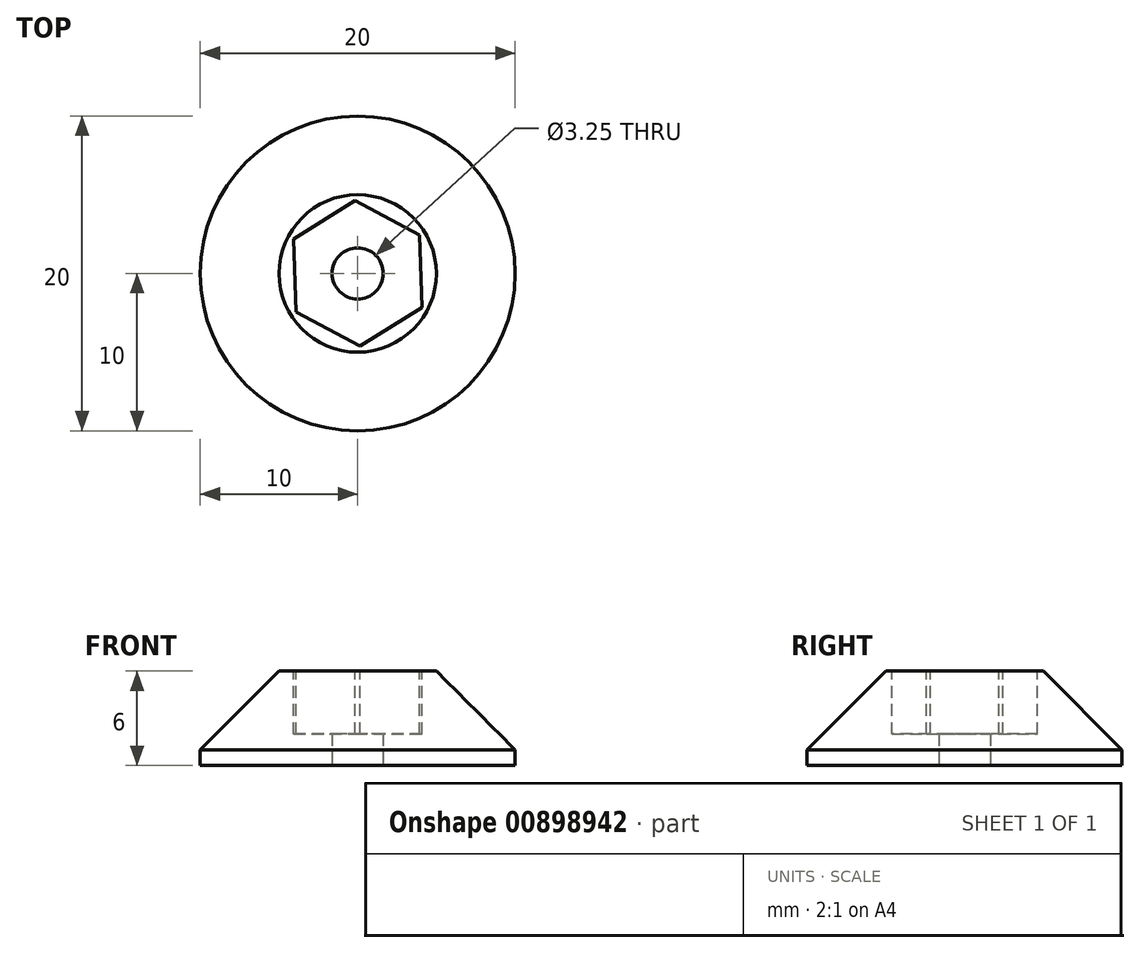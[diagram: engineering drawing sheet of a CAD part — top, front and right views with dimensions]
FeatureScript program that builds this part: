
annotation { "Feature Type Name" : "Feature", "Feature Type Description" : "" }
export const myFeature = defineFeature(function(context is Context, id is Id, definition is map)
    precondition{}
    {
        {
            var Q0;
            Q0=qCreatedBy(makeId("Top.planeOp"),FACE);
            var sketch = newSketch(context, id + "F0", { "sketchPlane" : qUnion([Q0])});
            skCircle(sketch, "E0", {"center": v(0, 0) * mm, "radius": 10 * mm});
            skSolve(sketch);
        }
        {
            var Q0;
            Q0 = qSketchRegion(id + "F0", true);
            extrude(context, id + "F1", {"entities" : qUnion([Q0]), "depth" : 6 * mm, "offsetDistance" : 25 * mm});
        }
        {
            var Q0;
            Q0=makeQuery(id+"F1.opExtrude","CAP_EDGE",EDGE,{"disambiguationData":[OSD([sQuery(id+"F0.wireOp",EDGE,"E0")])],"isStart":false});
            chamfer(context, id + "F2", {"entities" : qUnion([Q0]), "width" : 5 * mm, "tangentPropagation" : true});
        }
        {
            var Q0;
            Q0=makeQuery(id+"F1.opExtrude","CAP_FACE",FACE,{"disambiguationData":[OSD([sQuery(id+"F0.wireOp",EDGE,"E0")])],"isStart":false});
            var sketch = newSketch(context, id + "F3", { "sketchPlane" : qUnion([Q0])});
            skCircle(sketch, "E1.cCircle", {"center": v(0, 0) * mm, "radius": 4 * mm, "construction": true});
            skLineSegment(sketch, "E1.0", {"start": v(4.07, -2.18) * mm, "end": v(0.15, -4.62) * mm});
            skLineSegment(sketch, "E1.1", {"start": v(0.15, -4.62) * mm, "end": v(-3.92, -2.44) * mm});
            skLineSegment(sketch, "E1.2", {"start": v(-3.92, -2.44) * mm, "end": v(-4.07, 2.18) * mm});
            skLineSegment(sketch, "E1.3", {"start": v(-4.07, 2.18) * mm, "end": v(-0.15, 4.62) * mm});
            skLineSegment(sketch, "E1.4", {"start": v(-0.15, 4.62) * mm, "end": v(3.92, 2.44) * mm});
            skLineSegment(sketch, "E1.5", {"start": v(3.92, 2.44) * mm, "end": v(4.07, -2.18) * mm});
            skPoint(sketch, "E1.0.midPoint", {"position": v(2.11, -3.4) * mm});
            skSolve(sketch);
        }
        {
            var Q0;
            Q0=makeQuery(id+"F3.imprint","IMPRINT",FACE,{"disambiguationData":[TD([[makeQuery(id+"F3.imprint","IMPRINT",EDGE,{"derivedFrom":sQuery(id+"F3.wireOp",EDGE,"E1.0")}),-1.0]])]});
            extrude(context, id + "F4", {"entities" : qUnion([Q0]), "operationType" : NewBodyOperationType.REMOVE, "oppositeDirection" : true, "depth" : 4 * mm, "offsetDistance" : 25 * mm});
        }
        {
            var Q0;
            Q0=qCreatedBy(makeId("Top.planeOp"),FACE);
            var sketch = newSketch(context, id + "F5", { "sketchPlane" : qUnion([Q0])});
            skCircle(sketch, "E2", {"center": v(0, 0) * mm, "radius": 1.63 * mm});
            skSolve(sketch);
        }
        {
            var Q0;
            Q0 = qSketchRegion(id + "F5", true);
            extrude(context, id + "F6", {"entities" : qUnion([Q0]), "operationType" : NewBodyOperationType.REMOVE, "depth" : 5 * mm, "offsetDistance" : 25 * mm});
        }
    });
